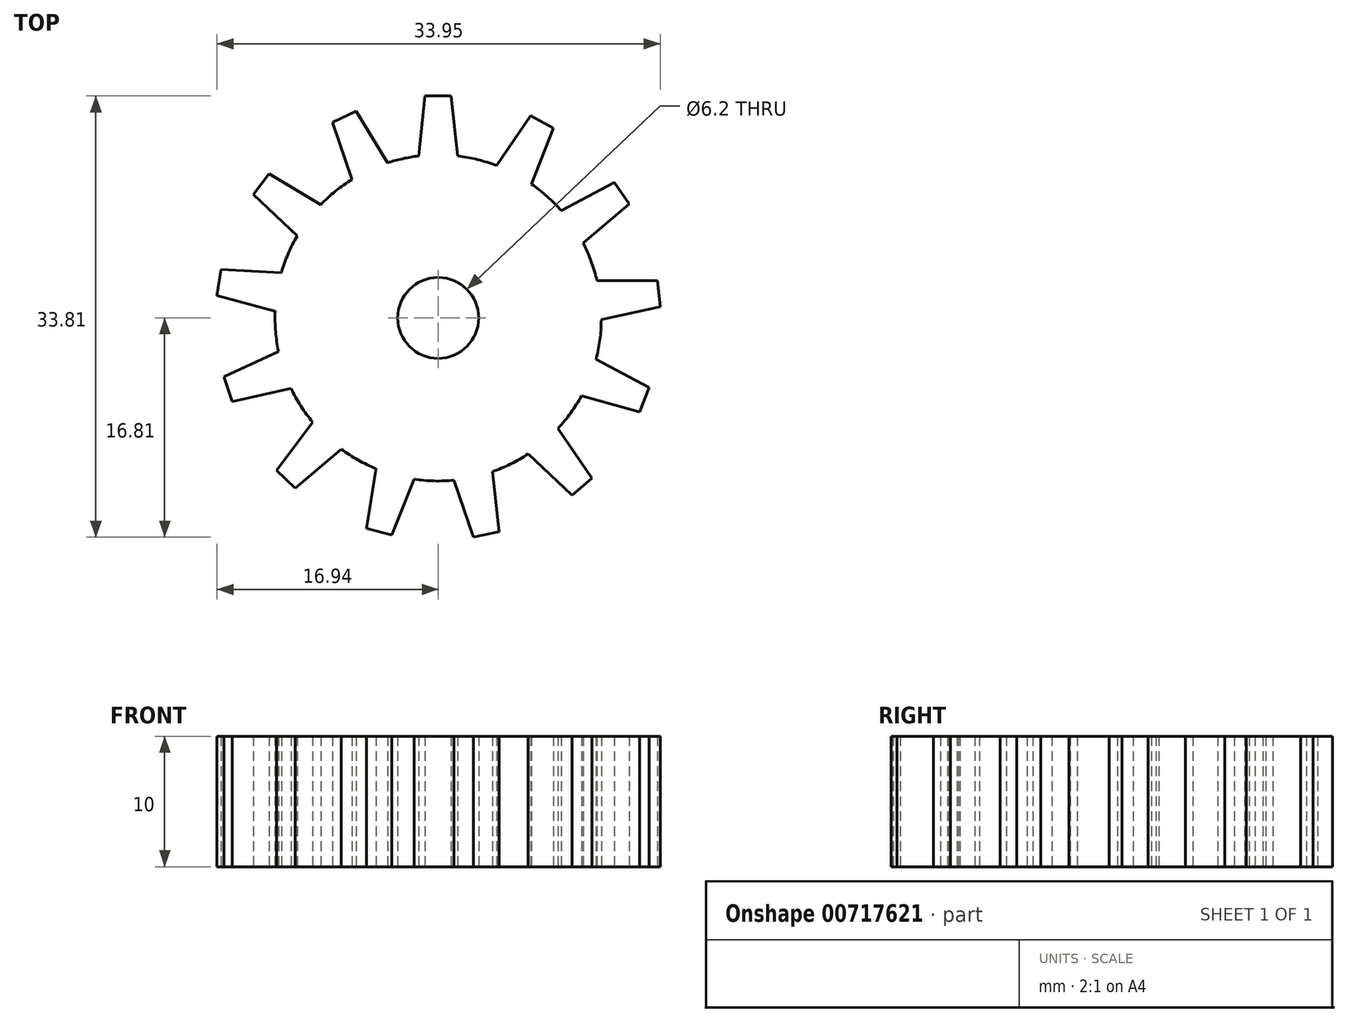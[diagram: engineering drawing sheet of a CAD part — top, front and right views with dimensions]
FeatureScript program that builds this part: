
annotation { "Feature Type Name" : "Feature", "Feature Type Description" : "" }
export const myFeature = defineFeature(function(context is Context, id is Id, definition is map)
    precondition{}
    {
        {
            var Q0;
            Q0=qCreatedBy(makeId("Top.planeOp"),FACE);
            var sketch = newSketch(context, id + "F0", { "sketchPlane" : qUnion([Q0])});
            skCircle(sketch, "E0", {"center": v(0, 0) * mm, "radius": 3.1 * mm});
            skCircle(sketch, "E1", {"center": v(0, 0) * mm, "radius": 12.5 * mm});
            skPoint(sketch, "E2", {"position": v(-1.5, 12.4) * mm});
            skPoint(sketch, "E3", {"position": v(1.5, 12.4) * mm});
            skPoint(sketch, "E4", {"position": v(-1, 17) * mm});
            skPoint(sketch, "E5", {"position": v(1, 17) * mm});
            skLineSegment(sketch, "E6", {"start": v(-1.5, 12.4) * mm, "end": v(1.5, 12.4) * mm});
            skLineSegment(sketch, "E7", {"start": v(1.5, 12.4) * mm, "end": v(1, 17) * mm});
            skLineSegment(sketch, "E8", {"start": v(1, 17) * mm, "end": v(-1, 17) * mm});
            skLineSegment(sketch, "E9", {"start": v(-1, 17) * mm, "end": v(-1.5, 12.4) * mm});
            skLineSegment(sketch, "E10.1.0", {"start": v(7.14, 10.26) * mm, "end": v(8.84, 14.55) * mm});
            skLineSegment(sketch, "E10.1.1", {"start": v(8.84, 14.55) * mm, "end": v(7.08, 15.49) * mm});
            skLineSegment(sketch, "E10.1.2", {"start": v(7.08, 15.49) * mm, "end": v(4.48, 11.67) * mm});
            skLineSegment(sketch, "E10.1.3", {"start": v(4.48, 11.67) * mm, "end": v(7.14, 10.26) * mm});
            skLineSegment(sketch, "E10.2.0", {"start": v(11.11, 5.73) * mm, "end": v(14.63, 8.72) * mm});
            skLineSegment(sketch, "E10.2.1", {"start": v(14.63, 8.72) * mm, "end": v(13.5, 10.37) * mm});
            skLineSegment(sketch, "E10.2.2", {"start": v(13.5, 10.37) * mm, "end": v(9.43, 8.21) * mm});
            skLineSegment(sketch, "E10.2.3", {"start": v(9.43, 8.21) * mm, "end": v(11.11, 5.73) * mm});
            skLineSegment(sketch, "E10.3.0", {"start": v(12.5, -0.14) * mm, "end": v(17, 0.86) * mm});
            skLineSegment(sketch, "E10.3.1", {"start": v(17, 0.86) * mm, "end": v(16.8, 2.84) * mm});
            skLineSegment(sketch, "E10.3.2", {"start": v(16.8, 2.84) * mm, "end": v(12.17, 2.84) * mm});
            skLineSegment(sketch, "E10.3.3", {"start": v(12.17, 2.84) * mm, "end": v(12.5, -0.14) * mm});
            skLineSegment(sketch, "E10.4.0", {"start": v(10.98, -5.98) * mm, "end": v(15.43, -7.2) * mm});
            skLineSegment(sketch, "E10.4.1", {"start": v(15.43, -7.2) * mm, "end": v(16.17, -5.35) * mm});
            skLineSegment(sketch, "E10.4.2", {"start": v(16.17, -5.35) * mm, "end": v(12.09, -3.19) * mm});
            skLineSegment(sketch, "E10.4.3", {"start": v(12.09, -3.19) * mm, "end": v(10.98, -5.98) * mm});
            skLineSegment(sketch, "E10.5.0", {"start": v(6.9, -10.42) * mm, "end": v(10.26, -13.6) * mm});
            skLineSegment(sketch, "E10.5.1", {"start": v(10.26, -13.6) * mm, "end": v(11.78, -12.3) * mm});
            skLineSegment(sketch, "E10.5.2", {"start": v(11.78, -12.3) * mm, "end": v(9.19, -8.48) * mm});
            skLineSegment(sketch, "E10.5.3", {"start": v(9.19, -8.48) * mm, "end": v(6.9, -10.42) * mm});
            skLineSegment(sketch, "E10.6.0", {"start": v(1.22, -12.44) * mm, "end": v(2.7, -16.81) * mm});
            skLineSegment(sketch, "E10.6.1", {"start": v(2.7, -16.81) * mm, "end": v(4.66, -16.38) * mm});
            skLineSegment(sketch, "E10.6.2", {"start": v(4.66, -16.38) * mm, "end": v(4.15, -11.8) * mm});
            skLineSegment(sketch, "E10.6.3", {"start": v(4.15, -11.8) * mm, "end": v(1.22, -12.44) * mm});
            skLineSegment(sketch, "E10.7.0", {"start": v(-4.74, -11.56) * mm, "end": v(-5.48, -16.12) * mm});
            skLineSegment(sketch, "E10.7.1", {"start": v(-5.48, -16.12) * mm, "end": v(-3.56, -16.65) * mm});
            skLineSegment(sketch, "E10.7.2", {"start": v(-3.56, -16.65) * mm, "end": v(-1.85, -12.36) * mm});
            skLineSegment(sketch, "E10.7.3", {"start": v(-1.85, -12.36) * mm, "end": v(-4.74, -11.56) * mm});
            skLineSegment(sketch, "E10.8.0", {"start": v(-9.6, -8) * mm, "end": v(-12.4, -11.68) * mm});
            skLineSegment(sketch, "E10.8.1", {"start": v(-12.4, -11.68) * mm, "end": v(-10.94, -13.05) * mm});
            skLineSegment(sketch, "E10.8.2", {"start": v(-10.94, -13.05) * mm, "end": v(-7.42, -10.06) * mm});
            skLineSegment(sketch, "E10.8.3", {"start": v(-7.42, -10.06) * mm, "end": v(-9.6, -8) * mm});
            skLineSegment(sketch, "E10.9.0", {"start": v(-12.23, -2.57) * mm, "end": v(-16.42, -4.52) * mm});
            skLineSegment(sketch, "E10.9.1", {"start": v(-16.42, -4.52) * mm, "end": v(-15.78, -6.41) * mm});
            skLineSegment(sketch, "E10.9.2", {"start": v(-15.78, -6.41) * mm, "end": v(-11.27, -5.4) * mm});
            skLineSegment(sketch, "E10.9.3", {"start": v(-11.27, -5.4) * mm, "end": v(-12.23, -2.57) * mm});
            skLineSegment(sketch, "E10.10.0", {"start": v(-12.01, 3.46) * mm, "end": v(-16.62, 3.7) * mm});
            skLineSegment(sketch, "E10.10.1", {"start": v(-16.62, 3.7) * mm, "end": v(-16.94, 1.72) * mm});
            skLineSegment(sketch, "E10.10.2", {"start": v(-16.94, 1.72) * mm, "end": v(-12.5, 0.5) * mm});
            skLineSegment(sketch, "E10.10.3", {"start": v(-12.5, 0.5) * mm, "end": v(-12.01, 3.46) * mm});
            skLineSegment(sketch, "E10.11.0", {"start": v(-9, 8.68) * mm, "end": v(-12.96, 11.05) * mm});
            skLineSegment(sketch, "E10.11.1", {"start": v(-12.96, 11.05) * mm, "end": v(-14.16, 9.45) * mm});
            skLineSegment(sketch, "E10.11.2", {"start": v(-14.16, 9.45) * mm, "end": v(-10.8, 6.29) * mm});
            skLineSegment(sketch, "E10.11.3", {"start": v(-10.8, 6.29) * mm, "end": v(-9, 8.68) * mm});
            skLineSegment(sketch, "E10.12.0", {"start": v(-3.89, 11.88) * mm, "end": v(-6.28, 15.83) * mm});
            skLineSegment(sketch, "E10.12.1", {"start": v(-6.28, 15.83) * mm, "end": v(-8.1, 14.98) * mm});
            skLineSegment(sketch, "E10.12.2", {"start": v(-8.1, 14.98) * mm, "end": v(-6.6, 10.61) * mm});
            skLineSegment(sketch, "E10.12.3", {"start": v(-6.6, 10.61) * mm, "end": v(-3.89, 11.88) * mm});
            skLineSegment(sketch, "E10.anchor1", {"start": v(0, 0) * mm, "end": v(1.5, 12.4) * mm, "construction": true});
            skLineSegment(sketch, "E10.anchor2", {"start": v(0, 0) * mm, "end": v(-3.89, 11.88) * mm, "construction": true});
            skSolve(sketch);
        }
        {
            var Q0;
            {var subQ1=sQuery(id+"F0.wireOp",EDGE,"E10.5.0");Q0=makeQuery(id+"F0.imprint","IMPRINT",FACE,{"disambiguationData":[TD([[makeQuery(id+"F0.imprint","IMPRINT",EDGE,{"derivedFrom":subQ1}),1.0]])]});}
            var Q1;
            {var subQ1=sQuery(id+"F0.wireOp",EDGE,"E10.2.0");Q1=makeQuery(id+"F0.imprint","IMPRINT",FACE,{"disambiguationData":[TD([[makeQuery(id+"F0.imprint","IMPRINT",EDGE,{"derivedFrom":subQ1}),1.0]])]});}
            var Q2;
            {var subQ1=sQuery(id+"F0.wireOp",EDGE,"E10.4.0");Q2=makeQuery(id+"F0.imprint","IMPRINT",FACE,{"disambiguationData":[TD([[makeQuery(id+"F0.imprint","IMPRINT",EDGE,{"derivedFrom":subQ1}),1.0]])]});}
            var Q3;
            {var subQ1=sQuery(id+"F0.wireOp",EDGE,"E10.13.0");Q3=makeQuery(id+"F0.imprint","IMPRINT",FACE,{"disambiguationData":[TD([[makeQuery(id+"F0.imprint","IMPRINT",EDGE,{"derivedFrom":subQ1}),1.0]])]});}
            var Q4;
            {var subQ1=sQuery(id+"F0.wireOp",EDGE,"E10.12.0");Q4=makeQuery(id+"F0.imprint","IMPRINT",FACE,{"disambiguationData":[TD([[makeQuery(id+"F0.imprint","IMPRINT",EDGE,{"derivedFrom":subQ1}),1.0]])]});}
            var Q5;
            {var subQ1=sQuery(id+"F0.wireOp",EDGE,"E10.8.0");Q5=makeQuery(id+"F0.imprint","IMPRINT",FACE,{"disambiguationData":[TD([[makeQuery(id+"F0.imprint","IMPRINT",EDGE,{"derivedFrom":subQ1}),1.0]])]});}
            var Q6;
            {var subQ1=sQuery(id+"F0.wireOp",EDGE,"E10.1.0");Q6=makeQuery(id+"F0.imprint","IMPRINT",FACE,{"disambiguationData":[TD([[makeQuery(id+"F0.imprint","IMPRINT",EDGE,{"derivedFrom":subQ1}),1.0]])]});}
            var Q7;
            {var subQ1=sQuery(id+"F0.wireOp",EDGE,"E10.11.0");Q7=makeQuery(id+"F0.imprint","IMPRINT",FACE,{"disambiguationData":[TD([[makeQuery(id+"F0.imprint","IMPRINT",EDGE,{"derivedFrom":subQ1}),1.0]])]});}
            var Q8;
            {var subQ1=sQuery(id+"F0.wireOp",EDGE,"E10.7.0");Q8=makeQuery(id+"F0.imprint","IMPRINT",FACE,{"disambiguationData":[TD([[makeQuery(id+"F0.imprint","IMPRINT",EDGE,{"derivedFrom":subQ1}),1.0]])]});}
            var Q9;
            {var subQ1=sQuery(id+"F0.wireOp",EDGE,"E10.10.0");Q9=makeQuery(id+"F0.imprint","IMPRINT",FACE,{"disambiguationData":[TD([[makeQuery(id+"F0.imprint","IMPRINT",EDGE,{"derivedFrom":subQ1}),1.0]])]});}
            var Q10;
            {var subQ1=sQuery(id+"F0.wireOp",EDGE,"E10.9.0");Q10=makeQuery(id+"F0.imprint","IMPRINT",FACE,{"disambiguationData":[TD([[makeQuery(id+"F0.imprint","IMPRINT",EDGE,{"derivedFrom":subQ1}),1.0]])]});}
            var Q11;
            {var subQ1=sQuery(id+"F0.wireOp",EDGE,"E10.14.0");Q11=makeQuery(id+"F0.imprint","IMPRINT",FACE,{"disambiguationData":[TD([[makeQuery(id+"F0.imprint","IMPRINT",EDGE,{"derivedFrom":subQ1}),1.0]])]});}
            var Q12;
            {var subQ1=sQuery(id+"F0.wireOp",EDGE,"E10.3.0");Q12=makeQuery(id+"F0.imprint","IMPRINT",FACE,{"disambiguationData":[TD([[makeQuery(id+"F0.imprint","IMPRINT",EDGE,{"derivedFrom":subQ1}),1.0]])]});}
            var Q13;
            {var subQ1=sQuery(id+"F0.wireOp",EDGE,"E10.6.0");Q13=makeQuery(id+"F0.imprint","IMPRINT",FACE,{"disambiguationData":[TD([[makeQuery(id+"F0.imprint","IMPRINT",EDGE,{"derivedFrom":subQ1}),1.0]])]});}
            var Q14;
            {var subQ3=sQuery(id+"F0.wireOp",EDGE,"E7");Q14=makeQuery(id+"F0.imprint","IMPRINT",FACE,{"disambiguationData":[TD([[makeQuery(id+"F0.imprint","IMPRINT",EDGE,{"derivedFrom":subQ3}),1.0]])]});}
            var Q15;
            {var subQ0=sQuery(id+"F0.wireOp",EDGE,"E10.7.3");Q15=makeQuery(id+"F0.imprint","IMPRINT",FACE,{"disambiguationData":[TD([[makeQuery(id+"F0.imprint","IMPRINT",EDGE,{"derivedFrom":subQ0}),1.0]])]});}
            var Q16;
            {var subQ0=sQuery(id+"F0.wireOp",EDGE,"E10.1.3");Q16=makeQuery(id+"F0.imprint","IMPRINT",FACE,{"disambiguationData":[TD([[makeQuery(id+"F0.imprint","IMPRINT",EDGE,{"derivedFrom":subQ0}),1.0]])]});}
            var Q17;
            {var subQ0=sQuery(id+"F0.wireOp",EDGE,"E10.11.3");Q17=makeQuery(id+"F0.imprint","IMPRINT",FACE,{"disambiguationData":[TD([[makeQuery(id+"F0.imprint","IMPRINT",EDGE,{"derivedFrom":subQ0}),1.0]])]});}
            var Q18;
            {var subQ0=sQuery(id+"F0.wireOp",EDGE,"E10.9.3");Q18=makeQuery(id+"F0.imprint","IMPRINT",FACE,{"disambiguationData":[TD([[makeQuery(id+"F0.imprint","IMPRINT",EDGE,{"derivedFrom":subQ0}),1.0]])]});}
            var Q19;
            {var subQ0=sQuery(id+"F0.wireOp",EDGE,"E10.4.3");Q19=makeQuery(id+"F0.imprint","IMPRINT",FACE,{"disambiguationData":[TD([[makeQuery(id+"F0.imprint","IMPRINT",EDGE,{"derivedFrom":subQ0}),1.0]])]});}
            var Q20;
            {var subQ0=sQuery(id+"F0.wireOp",EDGE,"E10.10.3");Q20=makeQuery(id+"F0.imprint","IMPRINT",FACE,{"disambiguationData":[TD([[makeQuery(id+"F0.imprint","IMPRINT",EDGE,{"derivedFrom":subQ0}),1.0]])]});}
            var Q21;
            {var subQ0=sQuery(id+"F0.wireOp",EDGE,"E10.8.3");Q21=makeQuery(id+"F0.imprint","IMPRINT",FACE,{"disambiguationData":[TD([[makeQuery(id+"F0.imprint","IMPRINT",EDGE,{"derivedFrom":subQ0}),1.0]])]});}
            var Q22;
            {var subQ0=sQuery(id+"F0.wireOp",EDGE,"E10.13.3");Q22=makeQuery(id+"F0.imprint","IMPRINT",FACE,{"disambiguationData":[TD([[makeQuery(id+"F0.imprint","IMPRINT",EDGE,{"derivedFrom":subQ0}),1.0]])]});}
            var Q23;
            {var subQ0=sQuery(id+"F0.wireOp",EDGE,"E10.3.3");Q23=makeQuery(id+"F0.imprint","IMPRINT",FACE,{"disambiguationData":[TD([[makeQuery(id+"F0.imprint","IMPRINT",EDGE,{"derivedFrom":subQ0}),1.0]])]});}
            var Q24;
            {var subQ0=sQuery(id+"F0.wireOp",EDGE,"E10.12.3");Q24=makeQuery(id+"F0.imprint","IMPRINT",FACE,{"disambiguationData":[TD([[makeQuery(id+"F0.imprint","IMPRINT",EDGE,{"derivedFrom":subQ0}),1.0]])]});}
            var Q25;
            {var subQ0=sQuery(id+"F0.wireOp",EDGE,"E10.6.3");Q25=makeQuery(id+"F0.imprint","IMPRINT",FACE,{"disambiguationData":[TD([[makeQuery(id+"F0.imprint","IMPRINT",EDGE,{"derivedFrom":subQ0}),1.0]])]});}
            var Q26;
            {var subQ0=sQuery(id+"F0.wireOp",EDGE,"E10.2.3");Q26=makeQuery(id+"F0.imprint","IMPRINT",FACE,{"disambiguationData":[TD([[makeQuery(id+"F0.imprint","IMPRINT",EDGE,{"derivedFrom":subQ0}),1.0]])]});}
            var Q27;
            {var subQ0=sQuery(id+"F0.wireOp",EDGE,"E10.5.3");Q27=makeQuery(id+"F0.imprint","IMPRINT",FACE,{"disambiguationData":[TD([[makeQuery(id+"F0.imprint","IMPRINT",EDGE,{"derivedFrom":subQ0}),1.0]])]});}
            var Q28;
            {var subQ0=sQuery(id+"F0.wireOp",EDGE,"E10.14.3");Q28=makeQuery(id+"F0.imprint","IMPRINT",FACE,{"disambiguationData":[TD([[makeQuery(id+"F0.imprint","IMPRINT",EDGE,{"derivedFrom":subQ0}),1.0]])]});}
            var Q29;
            {var subQ0=sQuery(id+"F0.wireOp",EDGE,"E6");Q29=makeQuery(id+"F0.imprint","IMPRINT",FACE,{"disambiguationData":[TD([[makeQuery(id+"F0.imprint","IMPRINT",EDGE,{"derivedFrom":subQ0}),1.0]])]});}
            var Q30;
            Q30=makeQuery(id+"F0.imprint","IMPRINT",FACE,{"disambiguationData":[TD([[makeQuery(id+"F0.imprint","IMPRINT",EDGE,{"derivedFrom":sQuery(id+"F0.wireOp",EDGE,"E0")}),-1.0]])]});
            extrude(context, id + "F1", {"entities" : qUnion([Q0, Q1, Q2, Q3, Q4, Q5, Q6, Q7, Q8, Q9, Q10, Q11, Q12, Q13, Q14, Q15, Q16, Q17, Q18, Q19, Q20, Q21, Q22, Q23, Q24, Q25, Q26, Q27, Q28, Q29, Q30]), "flatOperationType" : FlatOperationType.REMOVE, "depth" : 10 * mm, "offsetDistance" : 25 * mm, "domain" : OperationDomain.MODEL});
        }
    });
